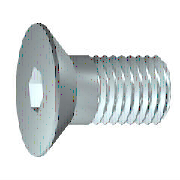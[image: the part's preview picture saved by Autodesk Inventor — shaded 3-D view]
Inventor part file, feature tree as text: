
AUTODESK INVENTOR PART (.ipt)
format: ipt  version: 2021 (Build 250183000, 183)  size: 194,560 bytes
history: native  units: mm (DEFAULTED — no unit token found)
features: other x4, sketch x3, fillet x1, chamfer x1
ambient origin geometry x8: Origin, YZ Plane, XZ Plane, XY Plane, X Axis, Y Axis, Z Axis, Center Point
bodies: Solid1 (feature_tree)
feature tree (9):
  sketch  "Sketch1"  dims[d2=3.0mm]
  other  "WorkPoint1"
  sketch  "Sketch2"  dims[d3=3.0mm]
  fillet  "Fillet1"  [1 undecoded]
  chamfer  "Chamfer1"  Distance=1.5mm
  other  "MSC_A1"
  other  "MSC_PF1"
  other  "MSC_PT1"
  sketch  "Sketch3"  dims[d4=1.5mm d5=1.5mm d6=8.0mm d7=6.0mm d8=360.0deg d9=0.0mm d10=2.0mm d11=2.0mm d12=120.0deg d13=120.0deg d14=120.0deg d15=120.0deg d16=1.2mm d17=0.0mm d18=0.1mm d19=0.25mm d20=45.0deg d22=0.0mm d23=0.0mm d35=0.0mm d37=0.0mm d38=0.0mm d39=0.25mm d40=0.0mm d41=0.0mm d42=0.0mm d43=45.0deg]
note: 1 required parameter value undecoded (feature->parameter linkage not recoverable at this tier; creation-order binding heuristic only, values carry confidence <= 0.55)
